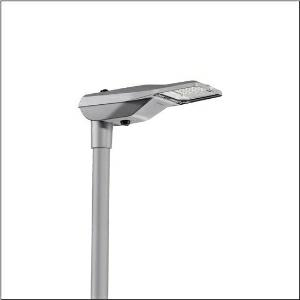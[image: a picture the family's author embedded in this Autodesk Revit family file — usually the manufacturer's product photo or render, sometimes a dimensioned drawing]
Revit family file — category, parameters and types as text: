
# Revit family: streetlight_sl_21_micro___stw1_0a_5xe1e43t08db_d620
name_source: partatom
category: Lighting Fixtures
units: mm (PartAtom-declared; Revit-internal decimal feet)

## family parameters
Cut with Voids When Loaded = No
Host = Face
Light Source = No
Part Type = Normal
Room Calculation Point = No
Round Connector Dimension = Use Diameter
Shared = No

## types (1)
- --- (1 x LED, 5320 lm, 39.1 W, 4000K)
    Apparent Load = 39 VA
    CIE Flux Codes = 38 75 98 100 100
    Color Rendering = 70
    Color Temperature = 4000K
    Default Elevation = 1800 mm
    Description = Streetlight SL 21 micro, mast luminaire, primary light control with lens, of PMMA, primary optical cover: cover, of toughened safety glass, transparent, light distribution: STW1.0a, light emission: direct distribution, primary light characteristic: asymmetric, installation type: side-entry, post-top, LED, High Power LED, rated luminous flux: 5.320lm, luminous efficacy: 136lm/W, light colour: 740, colour temperature: 4000K, control gear: D4i, control: flexible luminous flux parameterisation, time-dependent luminous flux control, constant luminous flux control, overheat protection, pre-setting: logarithmic dimming characteristic, mains connection: 220..240V, AC, 50/60Hz, start of lifetime: 39W, end of service life: 41W, reduction: 18W, luminaire housing, of diecast aluminium, powder-coated, Siteco® metallic grey (DB 702S), corrosivity category C5 mid according to DIN EN ISO 12944, please order mast flange separately, inclination adjustable: 0°, 5°, 10°, 15°, sealing non-destructively replaceable, multi-level sealing system, length: 528mm, width: 235mm, height: 110mm, mast flange for spigot size: 42mm (side-entry): 5XC10008XM4, 60/48mm (side-entry/post-top): 5XC10108XM2, 76/60mm (side-entry/post-top): 5XC10108XM1, Smart Interface below and above, protection rating (complete): IP66, insulation class (complete): insulation class II (safety insulation), certification: CE, ENEC, ENEC+, VDE, impact resistance: IK10, permissible operating ambient temperature for outdoor applications: -40..+50°C, standard-compliant lighting for roads and squares, packaging unit: 1 piece

Light Distribution: STW1.0a
    Height = 110 mm
    Lamp = 1 x LED
    Lamp Light Flux = 5320 lm
    Lamp Power = 39.1 W
    Lamp count = 1
    Length = 528 mm
    Luminous efficacy = 136 lm/W
    Manufacturer = Siteco
    ModVariant = No
    Model = 5XE1E43T08DB
    Number of Poles = 1
    OnlyDefault = Yes
    Power Factor = 1
    Product Name = Streetlight SL 21 micro | STW1.0a
    Product group = mast luminaire | pylon top
    ProductGroupID = 6100
    Protection Class = Protection class II
    Protection Degree = IP 66
    RLX_Detail_Level = 1
    RLX_Emergency_Light_Flux = 0 lm
    RLX_Emergency_Type = 0
    RLX_Emergency_Type_DB = No
    RlxData = <blob elided: 98457 chars, md5=a0e1c97a>
    Socket = socket
    Standby Power = 0 W
    System Light Flux = 5320 lm
    System Power = 39 W
    Type Comments = factory setting: luminous flux: 100 % | dim-lin: 254 | 765 mA
    Type Image = l_1007239.jpg
    URL = http://relux.com
    VarID = @adj_176713
    Voltage = 0 V
    Weight = 0.00 kg
    Width = 235 mm

## geometry (parser evidence)
native form markers: Blend x4, Sweep x12
no freeform markers — native parametric forms only
